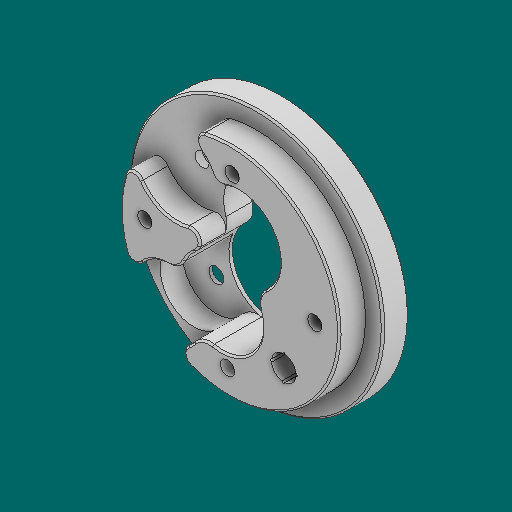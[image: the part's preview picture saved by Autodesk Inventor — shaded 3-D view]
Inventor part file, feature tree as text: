
AUTODESK INVENTOR PART (.ipt)
format: ipt  version: 2023.1 (Build 271208000, 208)  size: 317,952 bytes
history: native  units: in
note: dims shown in document units (in); Inventor stores cm internally (conversion verified against a paired STEP export)
features: sketch x6, other x3
ambient origin geometry x8: Origin, YZ Plane, XZ Plane, XY Plane, X Axis, Y Axis, Z Axis, Center Point
bodies: Solid1 (feature_tree)
feature tree (9):
  other  "UpperRingSeat.ipt"
  other  "Solid1::UpperRingSeat.ipt"
  other  "TaggingFeature1"
  sketch  "Sketch1"  dims[d0=0.3937in]
  sketch  "Sketch2"
  sketch  "Sketch3"
  sketch  "Sketch4"
  sketch  "Sketch5"
  sketch  "Sketch6"
